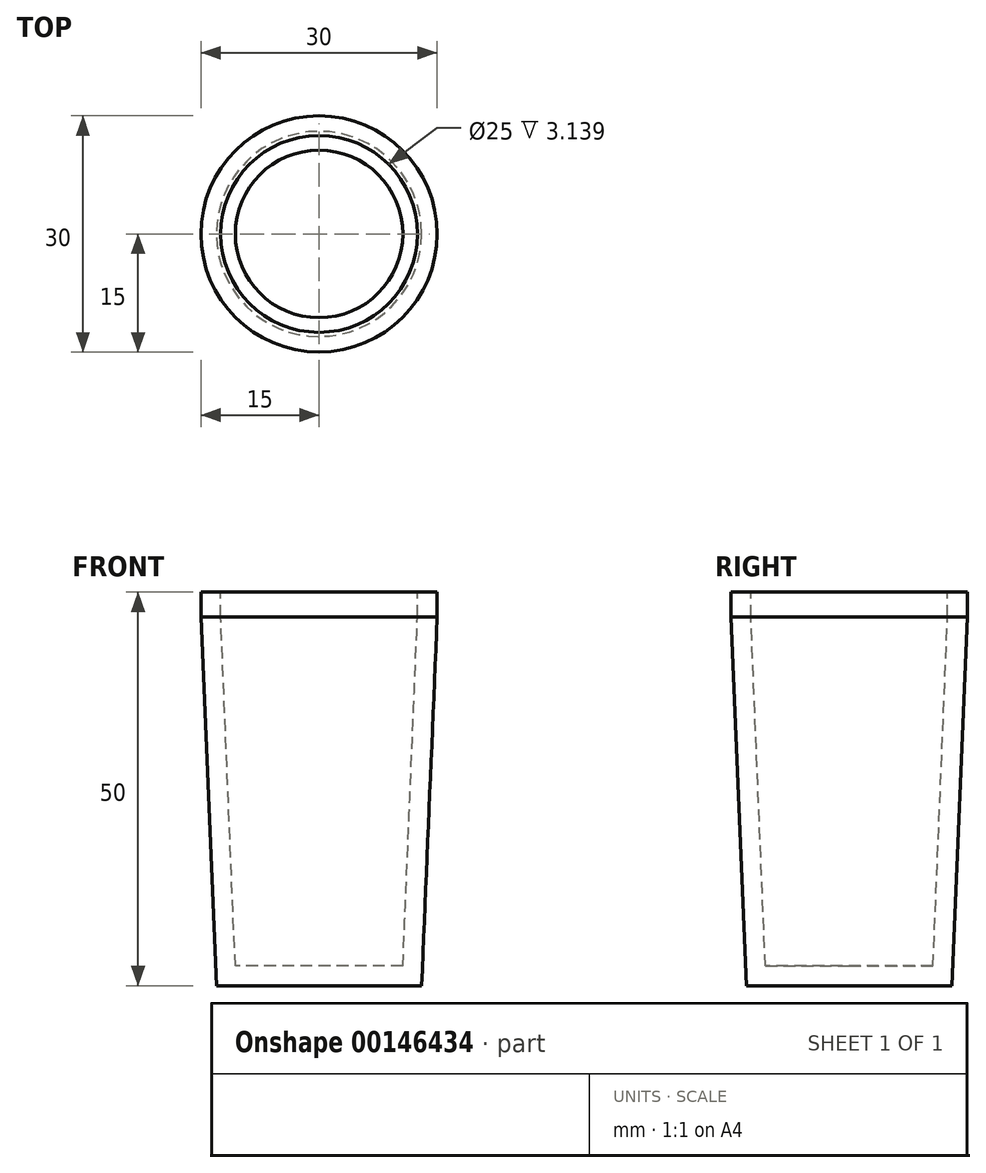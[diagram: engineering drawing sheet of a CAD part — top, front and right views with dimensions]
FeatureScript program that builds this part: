
annotation { "Feature Type Name" : "Feature", "Feature Type Description" : "" }
export const myFeature = defineFeature(function(context is Context, id is Id, definition is map)
    precondition{}
    {
        {
            var Q0;
            Q0=qCreatedBy(makeId("Right.planeOp"),FACE);
            var sketch = newSketch(context, id + "F0", { "sketchPlane" : qUnion([Q0])});
            skLineSegment(sketch, "E0", {"start": v(0, -97.7) * mm, "end": v(15, -97.7) * mm});
            skLineSegment(sketch, "E1", {"start": v(15, -97.7) * mm, "end": v(15, -100.89) * mm});
            skLineSegment(sketch, "E2", {"start": v(0, -97.7) * mm, "end": v(0, -147.7) * mm});
            skLineSegment(sketch, "E3", {"start": v(0, -147.7) * mm, "end": v(13.04, -147.7) * mm});
            skLineSegment(sketch, "E4", {"start": v(13.04, -147.7) * mm, "end": v(15, -100.89) * mm});
            skSolve(sketch);
        }
        {
            var Q0;
            Q0=makeQuery(id+"F0.imprint","IMPRINT",FACE,{"disambiguationData":[TD([[makeQuery(id+"F0.imprint","IMPRINT",EDGE,{"derivedFrom":sQuery(id+"F0.wireOp",EDGE,"E0")}),-1.0]])]});
            var Q1;
            Q1=sQuery(id+"F0.wireOp",EDGE,"E2");
            revolve(context, id + "F1", {"entities" : qUnion([Q0]), "axis" : qUnion([Q1]), "revolveType" : RevolveType.FULL});
        }
        {
            var Q0;
            Q0=makeQuery(id+"F1.opRevolve","SWEPT_FACE",FACE,{"disambiguationData":[OSD([sQuery(id+"F0.wireOp",EDGE,"E0")])]});
            shell(context, id + "F2", {"entities" : qUnion([Q0]), "thickness" : 2.5 * mm});
        }
    });
